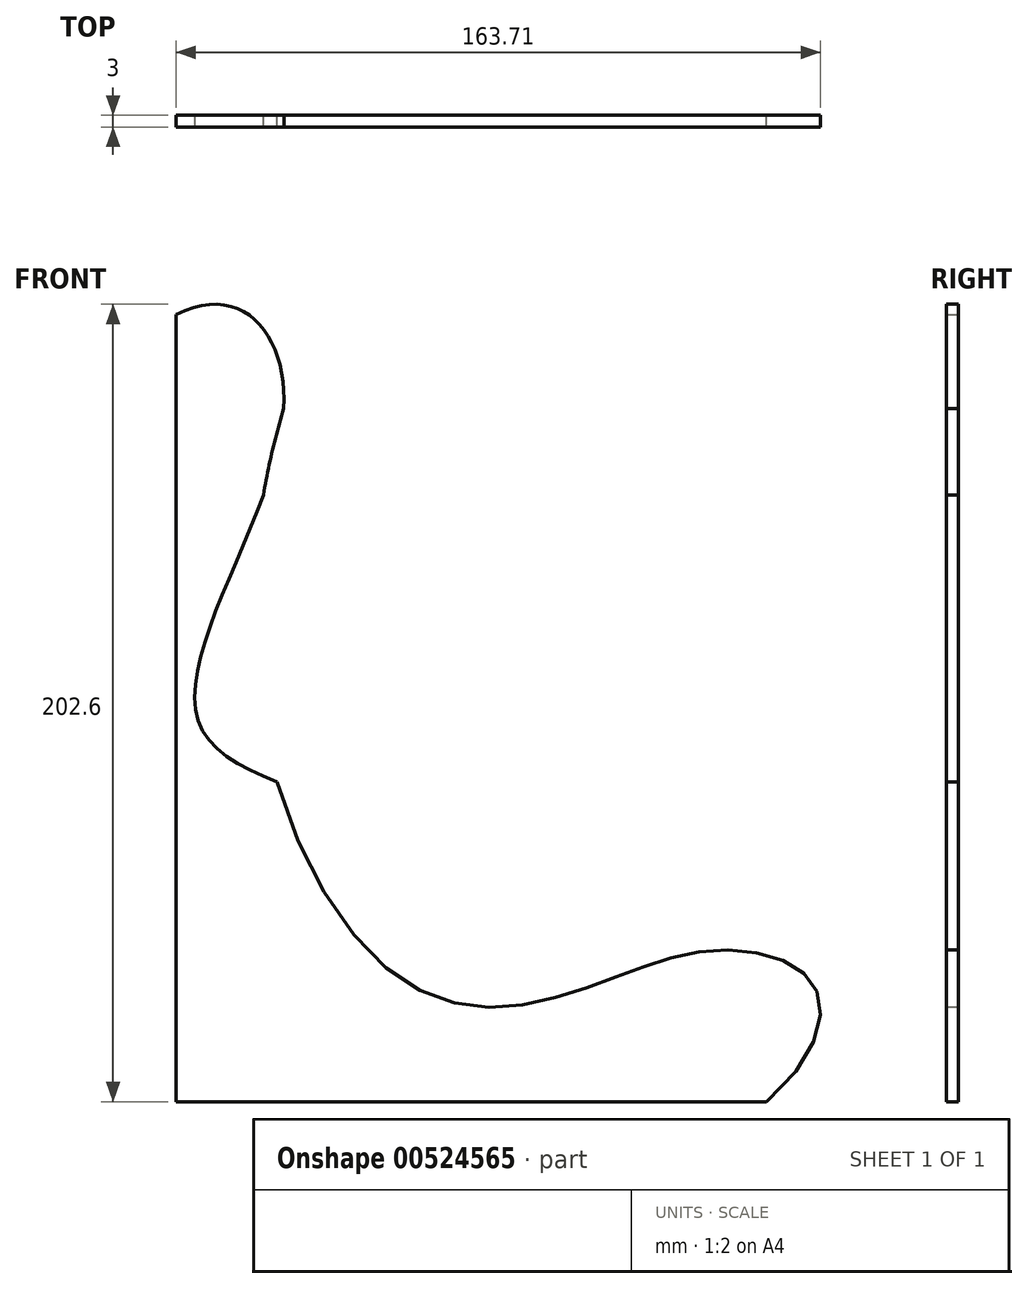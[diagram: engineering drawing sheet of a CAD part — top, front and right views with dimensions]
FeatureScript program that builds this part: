
annotation { "Feature Type Name" : "Feature", "Feature Type Description" : "" }
export const myFeature = defineFeature(function(context is Context, id is Id, definition is map)
    precondition{}
    {
        {
            var Q0;
            Q0=qCreatedBy(makeId("Front.planeOp"),FACE);
            var sketch = newSketch(context, id + "F0", { "sketchPlane" : qUnion([Q0])});
            skLineSegment(sketch, "E0", {"start": v(0, 200) * mm, "end": v(0, 0) * mm});
            skLineSegment(sketch, "E1", {"start": v(0, 0) * mm, "end": v(150, 0) * mm});
            skFitSpline(sketch, "E2", {"points": [v(27.36, 176.12) * mm, v(59.13, 29.83) * mm, v(103.5, 28.66) * mm, v(136.49, 38.41) * mm, v(161.52, 30.36) * mm, v(150, 0) * mm], "startDerivative": vector(-181.56, -605.16) * mm, "endDerivative": vector(-250.09, -215.85) * mm});
            skFitSpline(sketch, "E3", {"points": [v(0, 200) * mm, v(27.36, 176.12) * mm, v(6.55, 94.57) * mm, v(65.48, 61.1) * mm, v(67.92, 36.54) * mm], "startDerivative": vector(247.92, 123.08) * mm, "endDerivative": vector(-42.39, 8.57) * mm});
            skSolve(sketch);
        }
        {
            var Q0;
            Q0=makeQuery(id+"F0.imprint","IMPRINT",FACE,{"disambiguationData":[TD([[makeQuery(id+"F0.imprint","IMPRINT",EDGE,{"derivedFrom":sQuery(id+"F0.wireOp",EDGE,"E0")}),1.0]])]});
            extrude(context, id + "F1", {"entities" : qUnion([Q0]), "depth" : 3 * mm, "offsetDistance" : 25 * mm});
        }
    });
